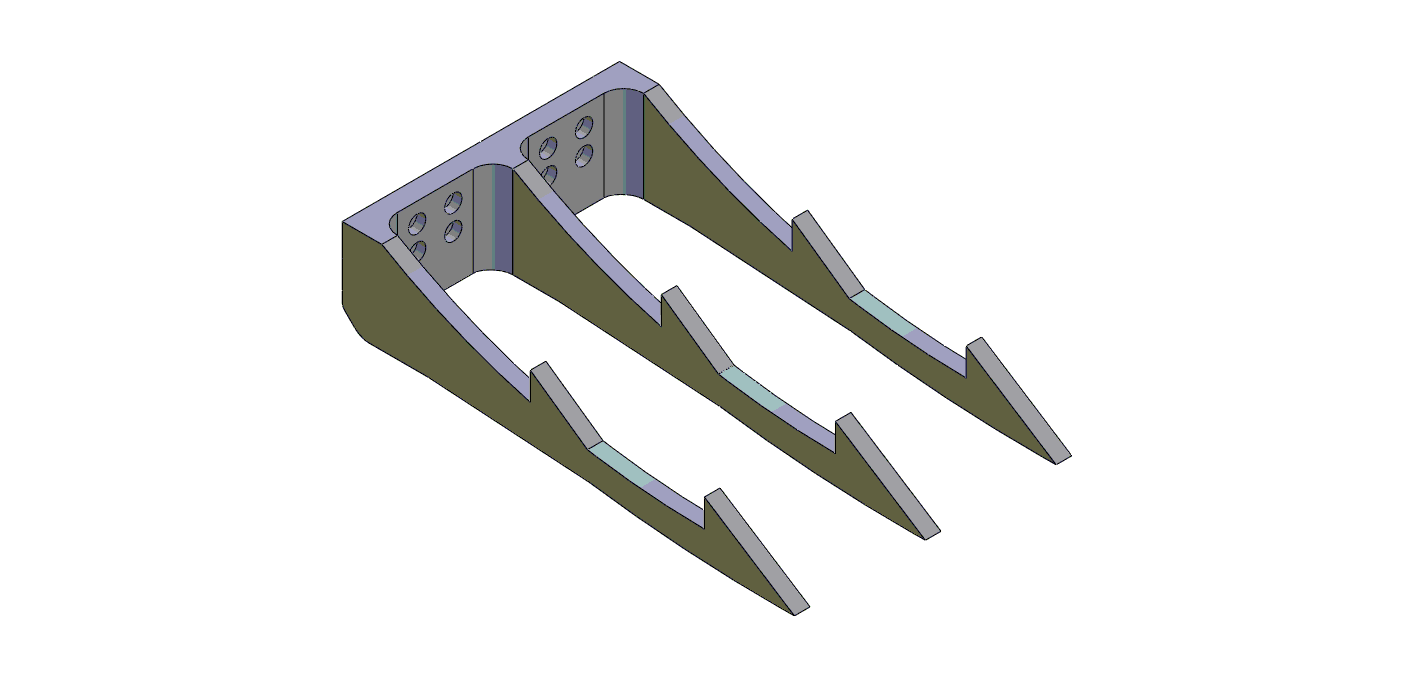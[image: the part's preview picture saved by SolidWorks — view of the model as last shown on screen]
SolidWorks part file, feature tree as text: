
SOLIDWORKS PART (.sldprt)
format: sldprt  version: not decoded by parser v0  size: 322,560 bytes
history: native  units: mm
features: sketch x6, extrude x2, plane x2, mirror x2, material x1, cut_extrude x1, fillet x1, hole x1 (+13 scaffold rows collapsed)
feature tree (29):
  scaffold x13  (default folders/planes/origin — collapsed)
  material  "Material <not specified>"
  sketch  "Sketch1"  dims[c1.D1=12.7mm c1.D2=6.35mm c1.D3=127.0mm c1.D4=25.4mm c1.D5=25.4mm c1.D6=25.4mm c1.D7=12.7mm c1.D8=25.4mm c1.D9=127.0mm c2.D1=25.4mm c2.D2=25.4mm c3.D1=25.4mm c3.D2=~30.660512mm c4.D1=12.7mm c4.D2=12.7mm c4.D3=12.7mm c4.D4=12.7mm c5.D3=8.89mm c5.D4=8.89mm]
  extrude  "Boss-Extrude1"  Depth=5mm
  sketch  "Sketch2"  dims[D1=20.574mm D2=6.35mm]
  extrude  "Boss-Extrude2"  Depth=88.9mm
  plane  "Plane1"  Offset=44.45mm
  mirror  "Mirror1"
  plane  "Plane2"  Offset=20.955mm
  mirror  "Mirror3"
  sketch  "Sketch8"
  cut_extrude  "Cut-Extrude2"  Depth=62.23mm
  fillet  "Fillet1"  Radius=6.35mm
  hole  "CBORE for #4 Socket Head Cap Screw1"  Diameter=2.2606mm Depth=6.331628mm
  sketch  "Sketch3"  dims[D1=6.35mm D2=6.35mm D3=6.35mm D4=6.35mm D5=6.35mm D6=6.35mm D7=6.35mm D8=6.35mm D9=6.35mm D10=6.35mm D11=6.35mm D12=6.35mm]
  sketch  "Sketch4"  dims[Thru Hole Dia.=2.2606mm Thru Hole Depth=~6.331628mm C'Bore Dia.=~5.55752mm C'Bore Depth=2.8448mm]
  sketch  "Sketch7"
decode coverage: 9 of 13 modeling features carry decoded parameters
note: ~ marks probable driven/reference dimensions
note: suppression state not decoded; provenance and decode notes live in map.json
